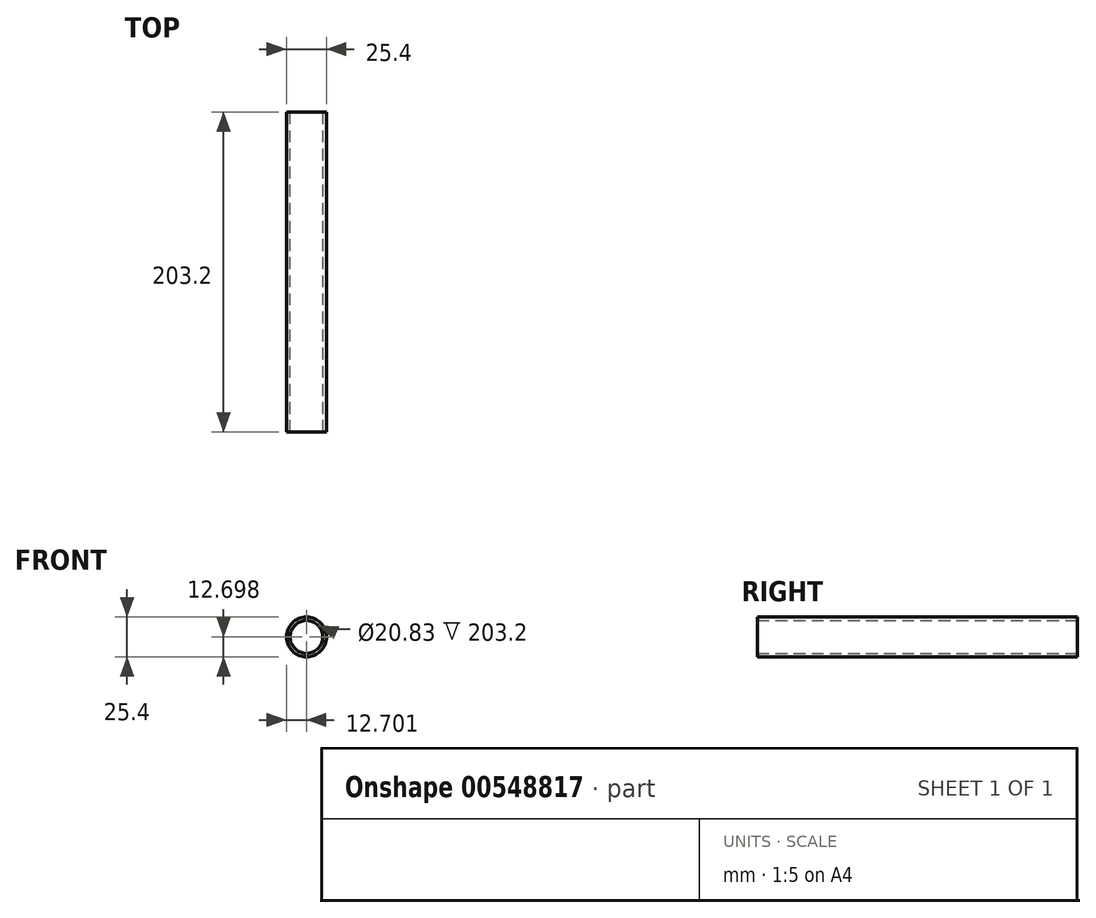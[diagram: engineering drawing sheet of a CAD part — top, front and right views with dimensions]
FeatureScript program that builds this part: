
annotation { "Feature Type Name" : "Feature", "Feature Type Description" : "" }
export const myFeature = defineFeature(function(context is Context, id is Id, definition is map)
    precondition{}
    {
        {
            var Q0;
            Q0=qCreatedBy(makeId("Front.planeOp"),FACE);
            var sketch = newSketch(context, id + "F0", { "sketchPlane" : qUnion([Q0])});
            skCircle(sketch, "E0", {"center": v(-34.32, 21.64) * mm, "radius": 10.41 * mm});
            skCircle(sketch, "E1", {"center": v(-34.32, 21.64) * mm, "radius": 12.7 * mm});
            skSolve(sketch);
        }
        {
            var Q0;
            Q0=makeQuery(id+"F0.imprint","IMPRINT",FACE,{"disambiguationData":[TD([[makeQuery(id+"F0.imprint","IMPRINT",EDGE,{"derivedFrom":sQuery(id+"F0.wireOp",EDGE,"E0")}),-1.0]])]});
            extrude(context, id + "F1", {"entities" : qUnion([Q0]), "endBound" : BoundingType.SYMMETRIC, "depth" : 203.2 * mm, "offsetDistance" : 25.4 * mm});
        }
    });
